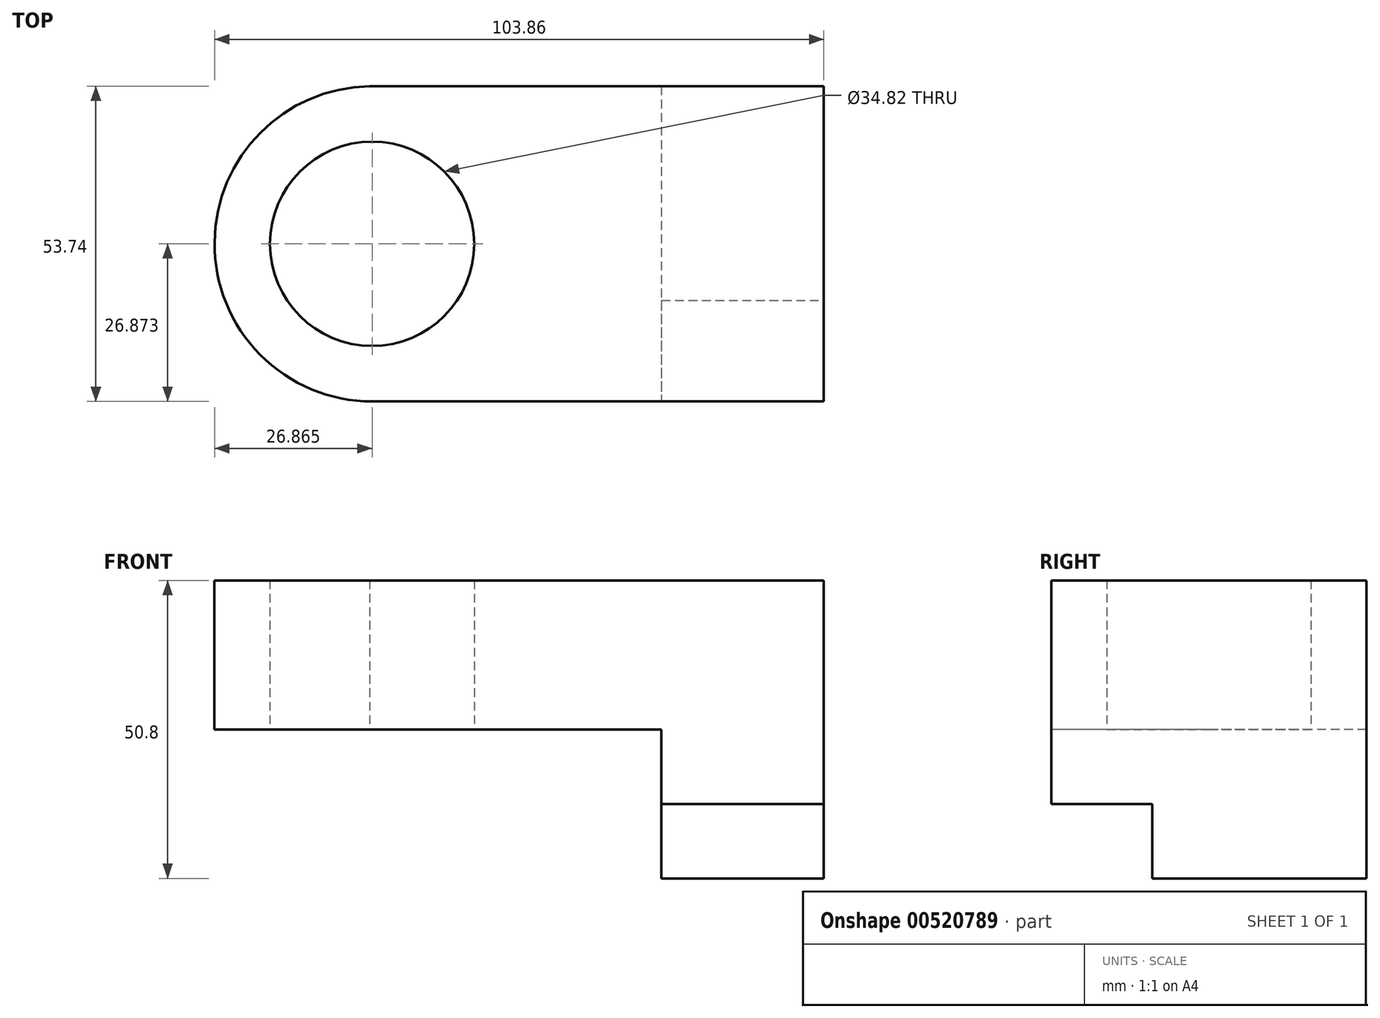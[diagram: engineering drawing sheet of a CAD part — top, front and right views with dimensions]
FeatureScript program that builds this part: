
annotation { "Feature Type Name" : "Feature", "Feature Type Description" : "" }
export const myFeature = defineFeature(function(context is Context, id is Id, definition is map)
    precondition{}
    {
        {
            var Q0;
            Q0=qCreatedBy(makeId("Top.planeOp"),FACE);
            var sketch = newSketch(context, id + "F0", { "sketchPlane" : qUnion([Q0])});
            skLineSegment(sketch, "E0", {"start": v(-35.3, -27.13) * mm, "end": v(41.7, -27.13) * mm});
            skLineSegment(sketch, "E1", {"start": v(41.7, -27.13) * mm, "end": v(41.7, 26.6) * mm});
            skLineSegment(sketch, "E2", {"start": v(41.7, 26.6) * mm, "end": v(-35.7, 26.6) * mm});
            skArc(sketch, "E3", {"start": v(-35.3, -27.13) * mm, "mid": v(-54.39, -19.17) * mm, "end": v(-62.16, 0) * mm});
            skArc(sketch, "E4", {"start": v(-62.16, 0) * mm, "mid": v(-54.35, 18.7) * mm, "end": v(-35.7, 26.6) * mm});
            skCircle(sketch, "E5", {"center": v(-35.3, -0.26) * mm, "radius": 17.4 * mm});
            skSolve(sketch);
        }
        {
            var Q0;
            Q0 = qSketchRegion(id + "F0", true);
            extrude(context, id + "F1", {"entities" : qUnion([Q0]), "depth" : 25.4 * mm, "offsetDistance" : 25.4 * mm});
        }
        {
            var Q0;
            Q0=makeQuery(id+"F1.opExtrude","CAP_FACE",FACE,{"disambiguationData":[OSD([sQuery(id+"F0.wireOp",EDGE,"E0"),sQuery(id+"F0.wireOp",EDGE,"E1"),sQuery(id+"F0.wireOp",EDGE,"E2"),sQuery(id+"F0.wireOp",EDGE,"E3"),sQuery(id+"F0.wireOp",EDGE,"E4"),sQuery(id+"F0.wireOp",EDGE,"E5")])],"isStart":true});
            var sketch = newSketch(context, id + "F2", { "sketchPlane" : qUnion([Q0])});
            skLineSegment(sketch, "E6.bottom", {"start": v(14.04, -26.6) * mm, "end": v(41.7, -26.6) * mm});
            skLineSegment(sketch, "E6.top", {"start": v(14.04, 27.13) * mm, "end": v(41.7, 27.13) * mm});
            skLineSegment(sketch, "E6.left", {"start": v(14.04, -26.6) * mm, "end": v(14.04, 27.13) * mm});
            skLineSegment(sketch, "E6.right", {"start": v(41.7, -26.6) * mm, "end": v(41.7, 27.13) * mm});
            skSolve(sketch);
        }
        {
            var Q0;
            Q0 = qSketchRegion(id + "F2", true);
            extrude(context, id + "F3", {"entities" : qUnion([Q0]), "operationType" : NewBodyOperationType.ADD, "depth" : 25.4 * mm, "offsetDistance" : 25.4 * mm});
        }
        {
            var Q0;
            Q0=makeQuery(id+"F3.opExtrude","CAP_FACE",FACE,{"disambiguationData":[OSD([sQuery(id+"F2.wireOp",EDGE,"E6.bottom"),sQuery(id+"F2.wireOp",EDGE,"E6.top"),sQuery(id+"F2.wireOp",EDGE,"E6.left"),sQuery(id+"F2.wireOp",EDGE,"E6.right")])],"isStart":false});
            var sketch = newSketch(context, id + "F4", { "sketchPlane" : qUnion([Q0])});
            skLineSegment(sketch, "E7.bottom", {"start": v(14.04, 27.13) * mm, "end": v(41.7, 27.13) * mm});
            skLineSegment(sketch, "E7.top", {"start": v(14.04, 9.88) * mm, "end": v(41.7, 9.88) * mm});
            skLineSegment(sketch, "E7.left", {"start": v(14.04, 27.13) * mm, "end": v(14.04, 9.88) * mm});
            skLineSegment(sketch, "E7.right", {"start": v(41.7, 27.13) * mm, "end": v(41.7, 9.88) * mm});
            skSolve(sketch);
        }
        {
            var Q0;
            Q0=makeQuery(id+"F4.imprint","IMPRINT",FACE,{"disambiguationData":[TD([[makeQuery(id+"F4.imprint","IMPRINT",EDGE,{"derivedFrom":sQuery(id+"F4.wireOp",EDGE,"E7.bottom")}),-1.0]])]});
            extrude(context, id + "F5", {"entities" : qUnion([Q0]), "operationType" : NewBodyOperationType.REMOVE, "oppositeDirection" : true, "depth" : 12.7 * mm, "offsetDistance" : 25.4 * mm});
        }
    });
